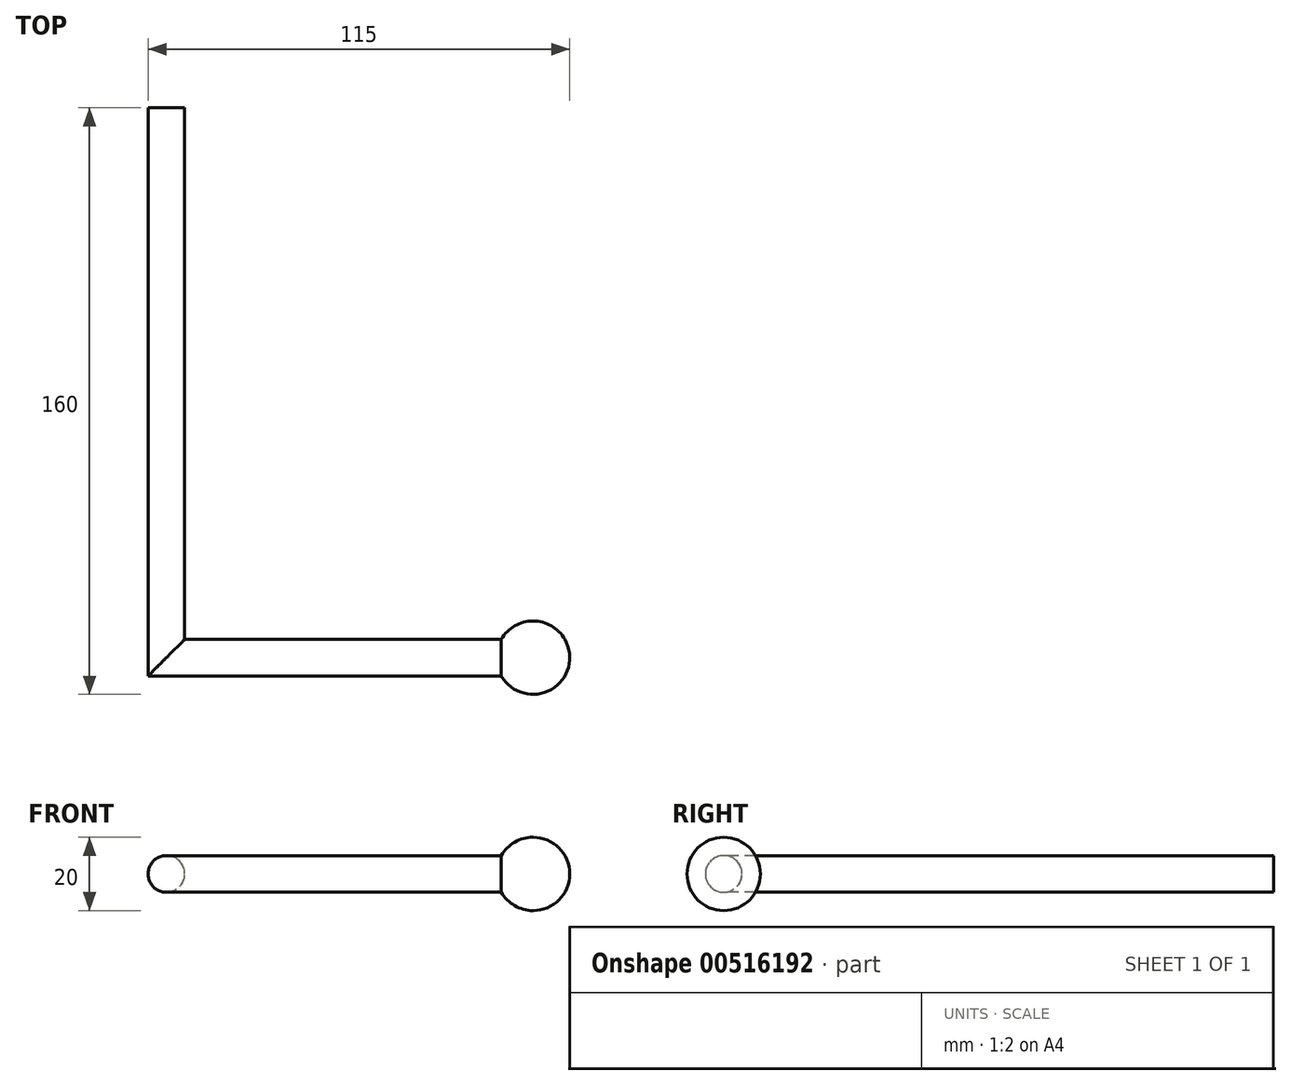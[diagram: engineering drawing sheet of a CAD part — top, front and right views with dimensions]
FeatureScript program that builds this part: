
annotation { "Feature Type Name" : "Feature", "Feature Type Description" : "" }
export const myFeature = defineFeature(function(context is Context, id is Id, definition is map)
    precondition{}
    {
        {
            var Q0;
            Q0=qCreatedBy(makeId("Top.planeOp"),FACE);
            var sketch = newSketch(context, id + "F0", { "sketchPlane" : qUnion([Q0])});
            skLineSegment(sketch, "E0", {"start": v(0, 0) * mm, "end": v(0, -150) * mm});
            skLineSegment(sketch, "E1", {"start": v(0, -150) * mm, "end": v(100, -150) * mm});
            skSolve(sketch);
        }
        {
            var Q0;
            Q0=qCreatedBy(makeId("Front.planeOp"),FACE);
            var sketch = newSketch(context, id + "F1", { "sketchPlane" : qUnion([Q0])});
            skCircle(sketch, "E2", {"center": v(0, 0) * mm, "radius": 5 * mm});
            skSolve(sketch);
        }
        {
            var Q0;
            Q0 = qSketchRegion(id + "F1", true);
            var Q1;
            Q1 = qConstructionFilter(qBodyType(qCreatedBy(id + "F0" ,EDGE), BodyType.WIRE), ConstructionObject.NO);
            sweep(context, id + "F2", {"profiles" : qUnion([Q0]), "path" : qUnion([Q1])});
        }
        {
            var Q0;
            Q0=makeQuery(id+"F2.opSweep","CAP_FACE",FACE,{"disambiguationData":[OSD([sQuery(id+"F0.wireOp",VERTEX,"E1.end"),sQuery(id+"F1.wireOp",EDGE,"E2")])],"isStart":false});
            var sketch = newSketch(context, id + "F3", { "sketchPlane" : qUnion([Q0])});
            skLineSegment(sketch, "E3", {"start": v(-150, 0) * mm, "end": v(-150, 10) * mm});
            skLineSegment(sketch, "E4", {"start": v(-150, 0) * mm, "end": v(-150, -10) * mm});
            skArc(sketch, "E5", {"start": v(-150, -10) * mm, "mid": v(-140, 0) * mm, "end": v(-150, 10) * mm});
            skSolve(sketch);
        }
        {
            var Q0;
            {var subQ0=sQuery(id+"F3.wireOp",EDGE,"E5");Q0=makeQuery(id+"F3.imprint","IMPRINT",FACE,{"disambiguationData":[TD([[makeQuery(id+"F3.imprint","IMPRINT",EDGE,{"derivedFrom":subQ0}),1.0]])]});}
            var Q1;
            {var subQ0=sQuery(id+"F3.wireOp",EDGE,"E4");var subQ1=sQuery(id+"F3.wireOp",EDGE,"E3");var subQ2=makeQuery(id+"F3.imprint","INTERSECT",VERTEX,{"derivedFrom":[subQ1,subQ0]});Q1=makeQuery(id+"F3.imprint","IMPRINT",FACE,{"disambiguationData":[TD([[makeQuery(id+"F3.imprint","IMPRINT",EDGE,{"disambiguationData":[TD([[subQ2,-1.0]])],"derivedFrom":subQ1}),-1.0]])]});}
            var Q2;
            Q2=sQuery(id+"F3.wireOp",EDGE,"E3");
            revolve(context, id + "F4", {"operationType" : NewBodyOperationType.ADD, "entities" : qUnion([Q0, Q1]), "axis" : qUnion([Q2]), "revolveType" : RevolveType.FULL});
        }
    });
